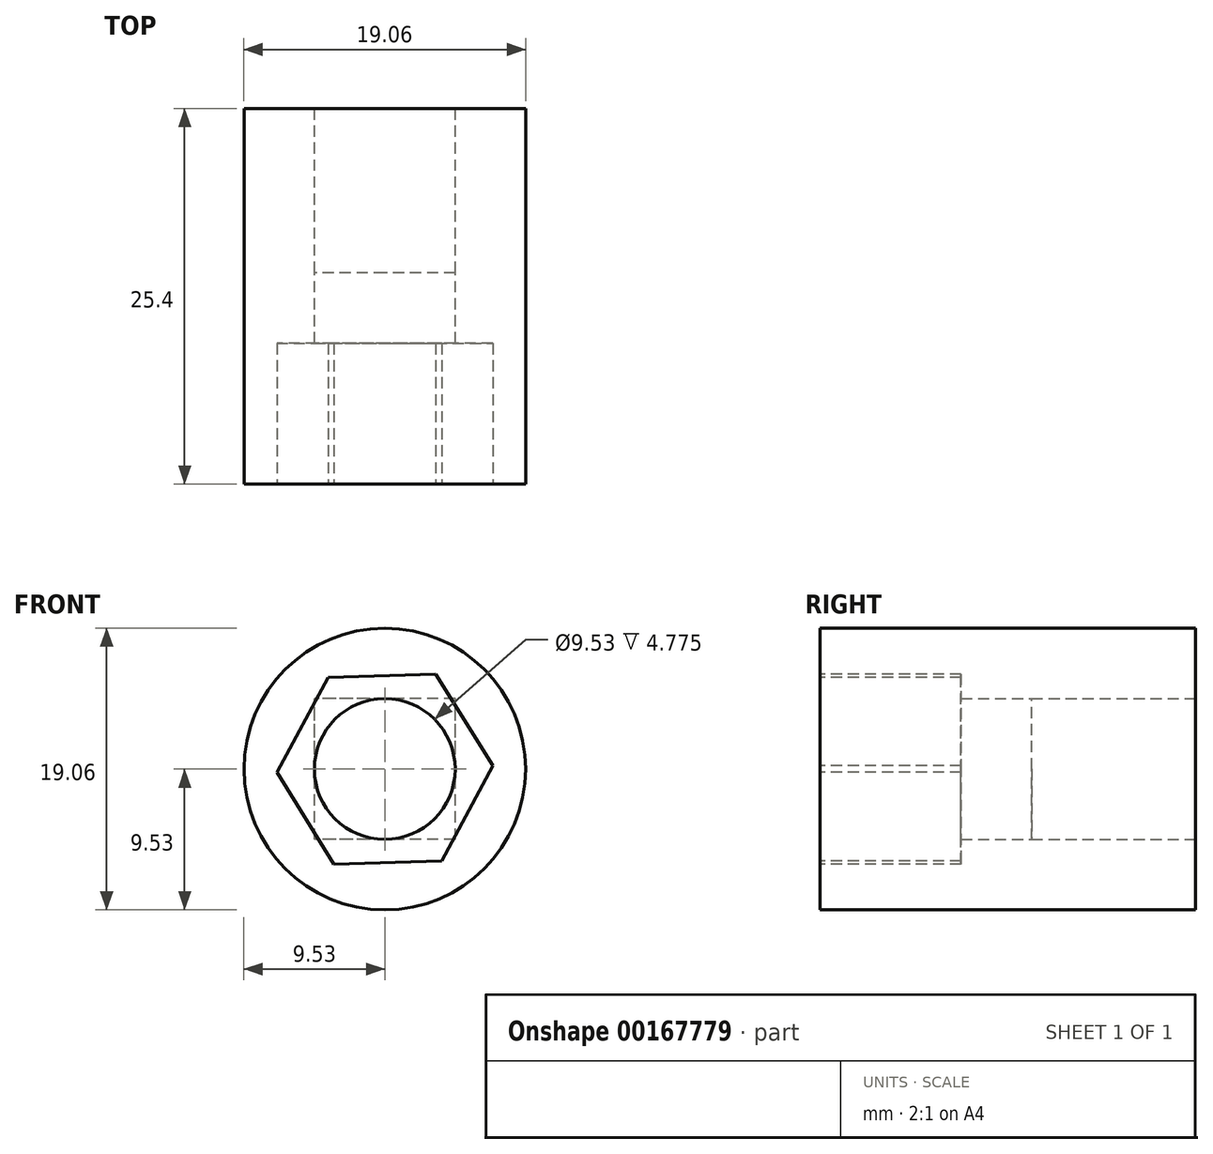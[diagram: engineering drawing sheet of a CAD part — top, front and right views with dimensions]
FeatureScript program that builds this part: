
annotation { "Feature Type Name" : "Feature", "Feature Type Description" : "" }
export const myFeature = defineFeature(function(context is Context, id is Id, definition is map)
    precondition{}
    {
        {
            var Q0;
            Q0=qCreatedBy(makeId("Front.planeOp"),FACE);
            var sketch = newSketch(context, id + "F0", { "sketchPlane" : qUnion([Q0])});
            skCircle(sketch, "E0", {"center": v(0, 0) * mm, "radius": 9.53 * mm});
            skSolve(sketch);
        }
        {
            var Q0;
            Q0=makeQuery(id+"F0.imprint","IMPRINT",FACE,{"disambiguationData":[TD([[makeQuery(id+"F0.imprint","IMPRINT",EDGE,{"derivedFrom":sQuery(id+"F0.wireOp",EDGE,"E0")}),1.0]])]});
            extrude(context, id + "F1", {"entities" : qUnion([Q0]), "depth" : 25.4 * mm});
        }
        {
            var Q0;
            Q0=qCreatedBy(makeId("Front.planeOp"),FACE);
            var sketch = newSketch(context, id + "F2", { "sketchPlane" : qUnion([Q0])});
            skLineSegment(sketch, "E1.bottom", {"start": v(4.76, -4.76) * mm, "end": v(-4.76, -4.76) * mm});
            skLineSegment(sketch, "E1.top", {"start": v(4.76, 4.76) * mm, "end": v(-4.76, 4.76) * mm});
            skLineSegment(sketch, "E1.left", {"start": v(4.76, -4.76) * mm, "end": v(4.76, 4.76) * mm});
            skLineSegment(sketch, "E1.right", {"start": v(-4.76, -4.76) * mm, "end": v(-4.76, 4.76) * mm});
            skPoint(sketch, "E1.middle", {"position": v(0, 0) * mm});
            skCircle(sketch, "E2", {"center": v(0, 0) * mm, "radius": 4.76 * mm});
            skSolve(sketch);
        }
        {
            var Q0;
            {var subQ0=sQuery(id+"F2.wireOp",EDGE,"E2");var subQ1=makeQuery(id+"F2.imprint","INTERSECT",VERTEX,{"derivedFrom":[sQuery(id+"F2.wireOp",EDGE,"E1.top"),subQ0]});Q0=makeQuery(id+"F2.imprint","IMPRINT",FACE,{"disambiguationData":[TD([[makeQuery(id+"F2.imprint","IMPRINT",EDGE,{"disambiguationData":[TD([[subQ1,1.0]])],"derivedFrom":subQ0}),1.0]])]});}
            var Q1;
            Q1=sQuery(id+"F2.wireOp",EDGE,"E2");
            extrude(context, id + "F3", {"entities" : qUnion([Q0]), "operationType" : NewBodyOperationType.REMOVE, "surfaceEntities" : qUnion([Q1]), "endBound" : BoundingType.THROUGH_ALL, "depth" : 25.4 * mm});
        }
        {
            var Q0;
            Q0 = qSketchRegion(id + "F2", true);
            extrude(context, id + "F4", {"entities" : qUnion([Q0]), "operationType" : NewBodyOperationType.REMOVE, "depth" : 11.1 * mm});
        }
        {
            var Q0;
            Q0=makeQuery(id+"F1.opExtrude","CAP_FACE",FACE,{"disambiguationData":[OSD([sQuery(id+"F0.wireOp",EDGE,"E0")])],"isStart":false});
            var sketch = newSketch(context, id + "F5", { "sketchPlane" : qUnion([Q0])});
            skCircle(sketch, "E3.cCircle", {"center": v(0, 0) * mm, "radius": 6.33 * mm, "construction": true});
            skLineSegment(sketch, "E3.0", {"start": v(3.46, 6.43) * mm, "end": v(7.3, 0.22) * mm});
            skLineSegment(sketch, "E3.1", {"start": v(7.3, 0.22) * mm, "end": v(3.84, -6.21) * mm});
            skLineSegment(sketch, "E3.2", {"start": v(3.84, -6.21) * mm, "end": v(-3.46, -6.43) * mm});
            skLineSegment(sketch, "E3.3", {"start": v(-3.46, -6.43) * mm, "end": v(-7.3, -0.22) * mm});
            skLineSegment(sketch, "E3.4", {"start": v(-7.3, -0.22) * mm, "end": v(-3.84, 6.21) * mm});
            skLineSegment(sketch, "E3.5", {"start": v(-3.84, 6.21) * mm, "end": v(3.46, 6.43) * mm});
            skPoint(sketch, "E3.0.midPoint", {"position": v(5.38, 3.33) * mm});
            skSolve(sketch);
        }
        {
            var Q0;
            Q0 = qSketchRegion(id + "F5", true);
            extrude(context, id + "F6", {"entities" : qUnion([Q0]), "operationType" : NewBodyOperationType.REMOVE, "oppositeDirection" : true, "depth" : 9.52 * mm});
        }
    });
